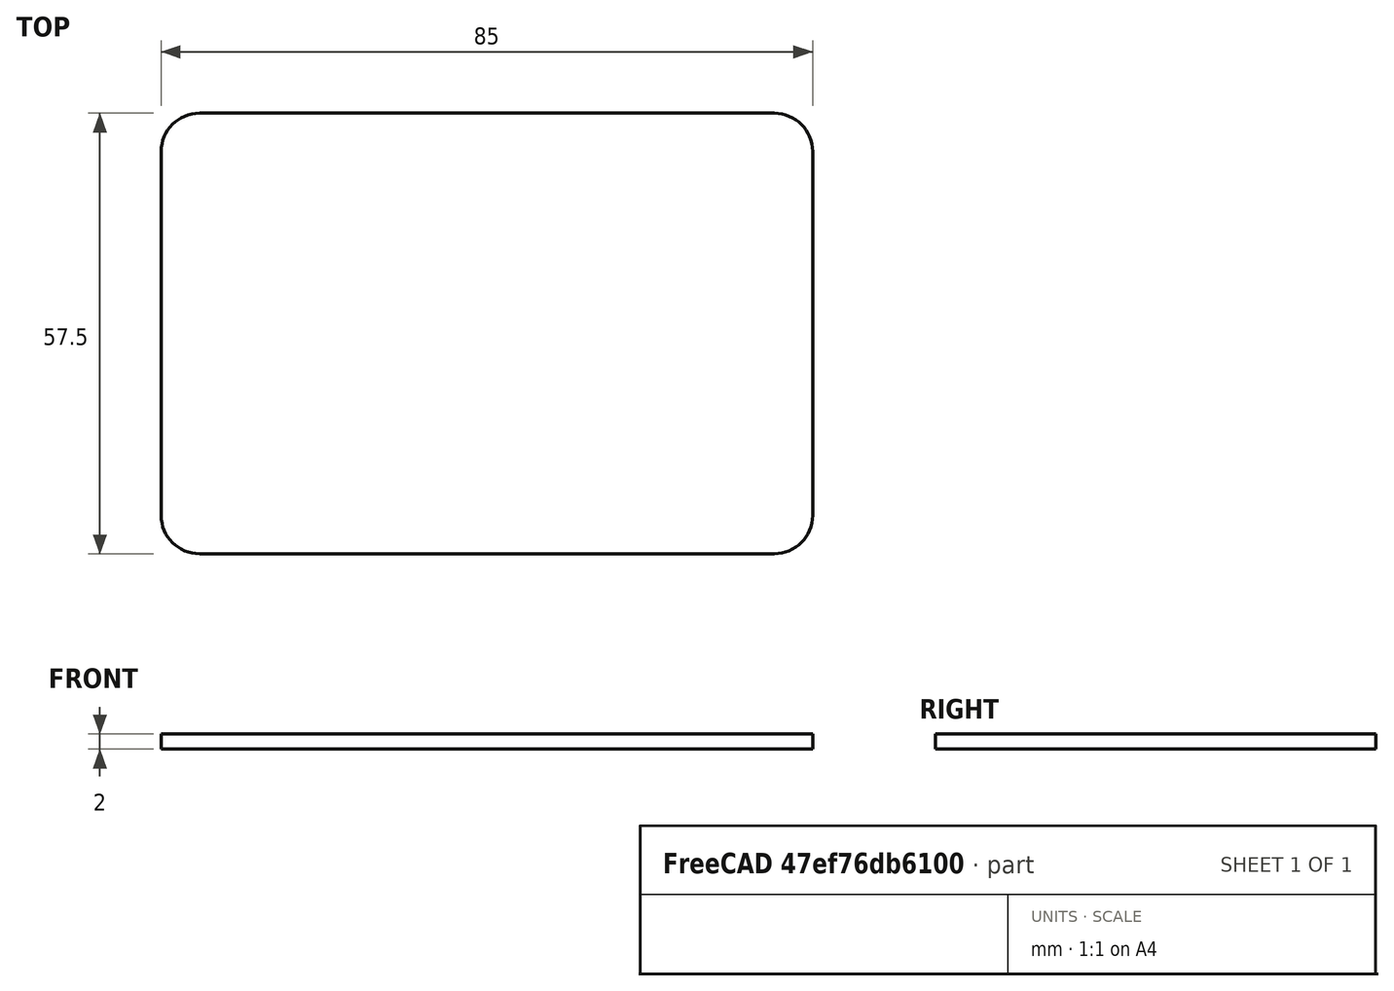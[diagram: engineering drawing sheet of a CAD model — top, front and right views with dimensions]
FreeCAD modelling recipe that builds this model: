
FCSTD DOCUMENT  (FreeCAD 0.21R33694 (Git))
Label: wiring cover
License: All rights reserved
LicenseURL: http://en.wikipedia.org/wiki/All_rights_reserved
objects: Sketcher::SketchObject×1, PartDesign::Pad×1, PartDesign::Body×1
note: 4 computed .brp shape members not serialized (recipe doc carries the construction recipe); baked Part::Feature solids carry a one-line shape summary decoded from their .brp

FEATURE [Sketcher::SketchObject] Sketch
  FullyConstrained = true
  MapMode = 5
  Support = -> [XY_Plane]
  sketch-geometry (10):
    g0: ArcOfCircle CenterX=-2.2e-15 CenterY=47.5 CenterZ=0 NormalX=0 NormalY=0 NormalZ=1 AngleXU=0 Radius=5 StartAngle=1.5708 EndAngle=3.14159
    g1: LineSegment StartX=2.20283e-11 StartY=52.5 StartZ=0 EndX=75 EndY=52.5 EndZ=0
    g2: ArcOfCircle CenterX=75 CenterY=47.5 CenterZ=0 NormalX=0 NormalY=0 NormalZ=1 AngleXU=0 Radius=5 StartAngle=-4.4054e-12 EndAngle=1.5708
    g3: LineSegment StartX=80 StartY=47.5 StartZ=0 EndX=80 EndY=2.20268e-11 EndZ=0
    g4: ArcOfCircle CenterX=75 CenterY=-1.8e-15 CenterZ=0 NormalX=0 NormalY=0 NormalZ=1 AngleXU=0 Radius=5 StartAngle=4.71239 EndAngle=6.28319
    g5: LineSegment StartX=75 StartY=-5 StartZ=0 EndX=1.9682e-11 EndY=-5 EndZ=0
    g6: ArcOfCircle CenterX=0 CenterY=0 CenterZ=0 NormalX=0 NormalY=0 NormalZ=1 AngleXU=0 Radius=5 StartAngle=3.14159 EndAngle=4.71239
    g7: LineSegment StartX=-5 StartY=1.96804e-11 StartZ=0 EndX=-5 EndY=47.5 EndZ=0
    g8: GeomPoint X=-5 Y=52.5 Z=0
    g9: GeomPoint X=80 Y=-5 Z=0
  constraints (23):
    c: Tangent(g0,g1) = 1.5708
    c: Tangent(g1,g2) = 1.5708
    c: Tangent(g2,g3) = 1.5708
    c: Tangent(g3,g4) = 1.5708
    c: Tangent(g4,g5) = 1.5708
    c: Tangent(g5,g6) = 1.5708
    c: Tangent(g6,g7) = 1.5708
    c: Tangent(g7,g0) = 1.5708
    c: Horizontal(g1)
    c: Horizontal(g5)
    c: Vertical(g3)
    c: Vertical(g7)
    c: Equal(g0,g2)
    c: Equal(g2,g4)
    c: Equal(g4,g6)
    c: PointOnObject(g8,g1)
    c: PointOnObject(g8,g7)
    c: PointOnObject(g9,g3)
    c: PointOnObject(g9,g5)
    c: Coincident(g6,g-1)
    c: DistanceY(g5,g0) = 57.5
    c: DistanceX(g0,g2) = 85
    c: Radius(g6) = 5
FEATURE [PartDesign::Pad] Pad
  Direction = (0,0,1)
  Length = 2
  Length2 = 10
  Profile = -> Sketch
  ReferenceAxis = -> Sketch [N_Axis]
  Refine = true
  Type = 0
FEATURE [PartDesign::Body] Body
  Group = -> [Sketch,Pad]
  Origin = -> Origin
  Tip = -> Pad
